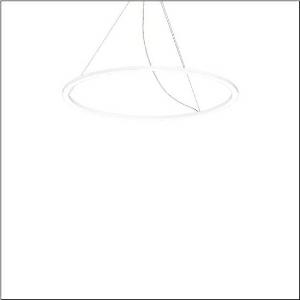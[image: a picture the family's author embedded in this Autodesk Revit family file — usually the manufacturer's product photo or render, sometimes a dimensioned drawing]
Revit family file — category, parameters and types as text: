
# Revit family: silica_r__21_ring-d_5pjbd3d1004a_5ef5
name_source: partatom
category: Lighting Fixtures
units: mm (PartAtom-declared; Revit-internal decimal feet)

## family parameters
Cut with Voids When Loaded = No
Host = Face
Light Source = No
Part Type = Normal
Room Calculation Point = No
Round Connector Dimension = Use Diameter
Shared = No

## types (1)
- Silica® 21 Ring-D (1 x LED, 8050 lm, 94 W, 3000K)
    Apparent Load = 94 VA
    CIE Flux Codes = 37 69 92 100 100
    Color Rendering = 80
    Color Temperature = 3000K
    Default Elevation = 1800 mm
    Description = Silica® 21 Ring-D, suspended luminaire, of PMMA, frosted, light emission: ring underside luminous distribution, primary light characteristic: symmetric, installation type: suspended mounting, LED, rated luminous flux: 8.050lm, luminous efficacy: 86lm/W, light colour: 830, colour temperature: 3000K, control gear: DALI 2, with terminal, 5-pole, mains connection: 230V, AC/DC, 0/50..60Hz, rated input power: 94W, housing, of extruded aluminium section, traffic white (RAL 9016), diameter: 1.100mm, ceiling canopy, traffic white (RAL 9016), protection rating (lamp compartment): IP40, insulation class (complete): insulation class I (protective earthing), certification: CE, impact resistance: IK02, permissible operating ambient temperature: 0..+35°C, packaging unit: 1 piece
    Height = 25 mm  [stored 0.082021 ft]
    Lamp = 1 x LED
    Lamp Light Flux = 8050 lm
    Lamp Power = 94 W
    Lamp count = 1
    Length = 1100 mm
    Luminous efficacy = 86 lm/W
    Manufacturer = Siteco
    ModVariant = No
    Model = 5PJBD3D1004A
    Mounting Place = Ceiling
    Mounting Type = Pendant
    Number of Poles = 1
    OnlyDefault = Yes
    Power Factor = 1
    Product Name = Silica® 21 Ring-D
    Product group = suspended luminaire
    ProductGroupID = 905
    Protection Class = Protection class I
    Protection Degree = IP 40
    RLX_Detail_Level = 1
    RLX_Emergency_Light_Flux = 0 lm
    RLX_Emergency_Type = 0
    RLX_Emergency_Type_DB = No
    RlxData = <blob elided: 12521 chars, md5=37edd733>
    Socket = socket
    Standby Power = 0 W
    System Light Flux = 8050 lm
    System Power = 94 W
    Type Comments = Product without accessories
    Type Image = l_1258355.jpg
    URL = http://relux.com
    VarID = ---
    Voltage = 0 V
    Weight = 0.00 kg
    Width = 0 mm  [stored 0 ft]

note: [stored X ft] marks values corroborated as IEEE doubles in the binary element streams (Revit-internal decimal feet)

## geometry (parser evidence)
native form markers: Sweep x8
no freeform markers — native parametric forms only
